FCSTD DOCUMENT  (FreeCAD 0.16R6712 (Git))
Label: MT-QA geometry
License: All rights reserved
LicenseURL: http://en.wikipedia.org/wiki/All_rights_reserved
objects: Sketcher::SketchObject×1
note: 1 computed .brp shape members not serialized (recipe doc carries the construction recipe); baked Part::Feature solids carry a one-line shape summary decoded from their .brp

FEATURE [Sketcher::SketchObject] Sketch
  sketch-geometry (6):
    g0: LineSegment [constr] StartX=250.893 StartY=144.853 StartZ=0 EndX=0 EndY=0 EndZ=0
    g1: LineSegment [constr] StartX=0 StartY=0 StartZ=0 EndX=-914.893 EndY=0 EndZ=0
    g2: LineSegment [constr] StartX=0 StartY=0 StartZ=0 EndX=-221.928 EndY=186.219 EndZ=0
    g3: LineSegment [constr] StartX=-914.893 StartY=0 StartZ=0 EndX=-221.928 EndY=186.219 EndZ=0
    g4: LineSegment [constr] StartX=-914.893 StartY=0 StartZ=0 EndX=-202.818 EndY=88.4778 EndZ=0
    g5: LineSegment [constr] StartX=-202.818 StartY=88.4778 StartZ=0 EndX=250.893 EndY=144.853 EndZ=0
  constraints (17):
    c: PointOnObject(g0,g-1)
    c: PointOnObject(g0,g-2)
    c: Coincident(g1,g-1)
    c: Horizontal(g1)
    c: Angle(g0,g1) = 2.61799
    c: Coincident(g2,g-1)
    c: Coincident(g3,g1)
    c: Coincident(g3,g2)
    c: Equal(g2,g0)
    c: Angle(g2,g1) = 0.698132
    c: Distance(g3) = 717.55
    c: Equal(g3,g4) = 666.75
    c: Coincident(g4,g1)
    c: Coincident(g4,g5)
    c: Parallel(g5,g4)
    c: Distance(g5) = 457.2
    c: Coincident(g5,g0)
